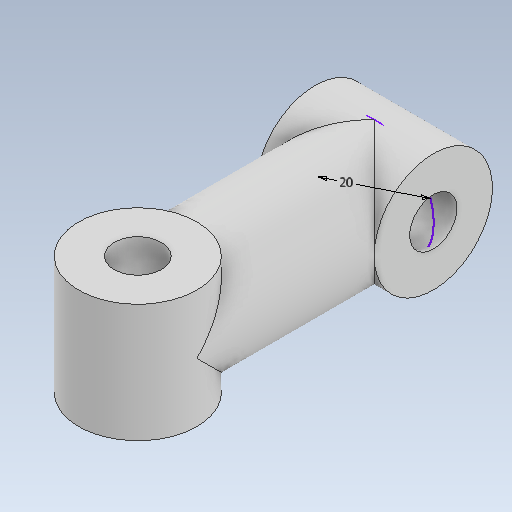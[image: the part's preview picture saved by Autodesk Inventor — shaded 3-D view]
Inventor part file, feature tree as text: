
AUTODESK INVENTOR PART (.ipt)
format: ipt  version: 2020 (Build 240168000, 168)  size: 165,376 bytes
history: native  units: mm
features: extrude x5, sketch x4, projected_geometry x3, plane x2
ambient origin geometry x8: Origin, YZ Plane, XZ Plane, XY Plane, X Axis, Y Axis, Z Axis, Center Point
bodies: Solid1 (feature_tree)
feature tree (14):
  plane  "Work Plane2"
  extrude  "Extrusion2"  Depth=20.0mm TaperAngle=0.0deg
  plane  "Work Plane1"
  extrude  "Extrusion3"  Depth=20.0mm
  extrude  "Extrusion4"  Depth=20.0mm
  extrude  "Extrusion8"  Depth=20.0mm
  extrude  "Extrusion9"  Depth=20.0mm TaperAngle=0.0deg
  sketch  "Sketch4"  dims[d7=20.0mm d8=40.0mm d9=0.0mm]
  sketch  "Sketch5"  dims[d11=-10.0mm d12=20.0mm]
  sketch  "Sketch9"  dims[d13=20.0mm d14=0.0mm d15=8.0mm]
  projected_geometry  "Projected Loop1"
  sketch  "Sketch10"  dims[d16=30.0mm d17=0.0mm d39=20.0mm d40=20.0mm d41=0.0mm d42=8.0mm d43=0.0mm d44=0.0mm]
  projected_geometry  "Project Cut Edges2"
  projected_geometry  "Project Cut Edges3"
